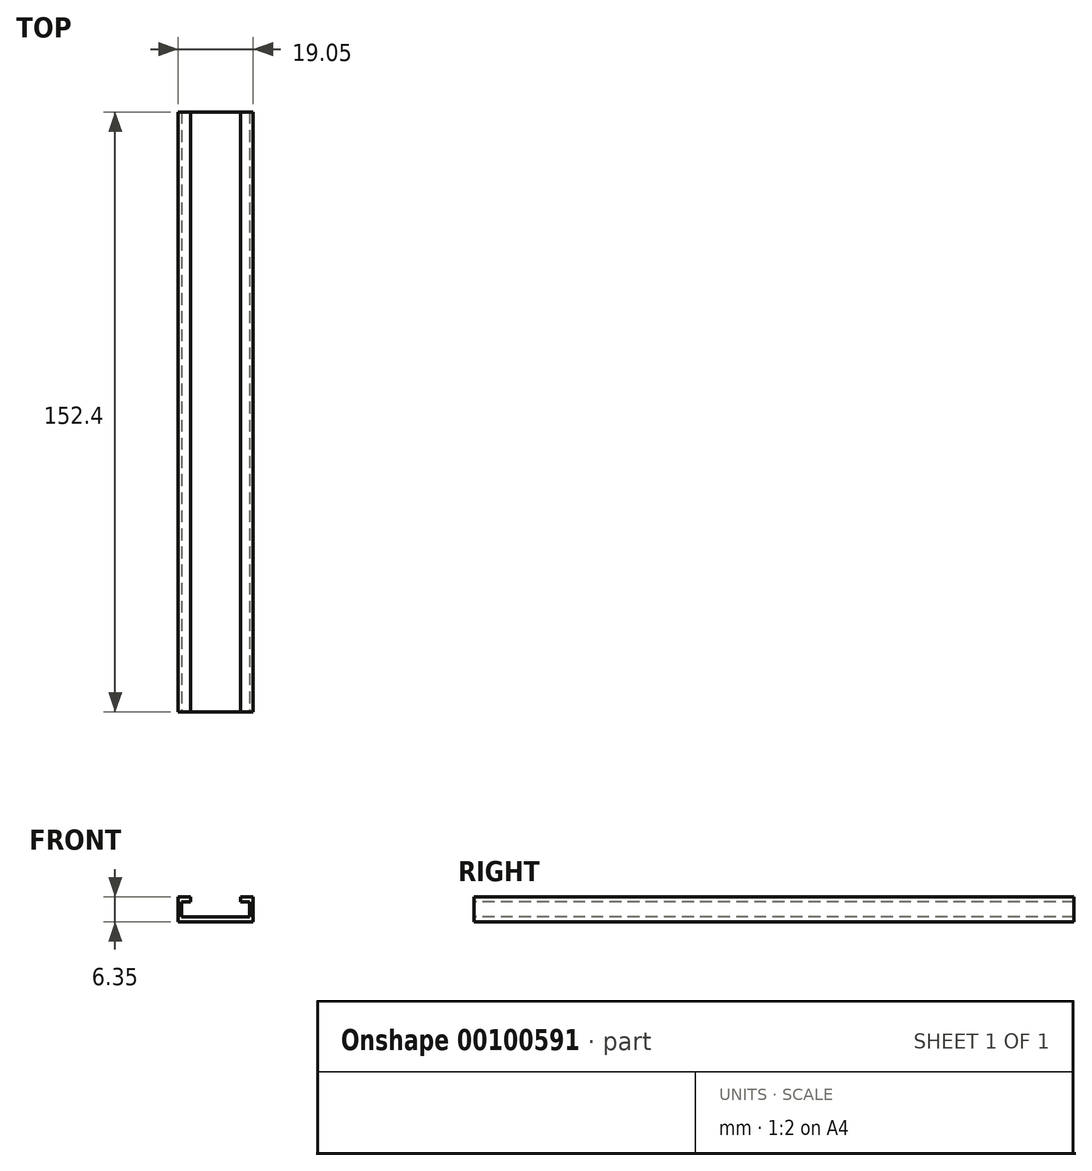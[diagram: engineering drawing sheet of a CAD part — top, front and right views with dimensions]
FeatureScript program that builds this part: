
annotation { "Feature Type Name" : "Feature", "Feature Type Description" : "" }
export const myFeature = defineFeature(function(context is Context, id is Id, definition is map)
    precondition{}
    {
        {
            var Q0;
            Q0=qCreatedBy(makeId("Top.planeOp"),FACE);
            var sketch = newSketch(context, id + "F0", { "sketchPlane" : qUnion([Q0])});
            skLineSegment(sketch, "E0.bottom", {"start": v(-36.41, -40.34) * mm, "end": v(-17.36, -40.34) * mm});
            skLineSegment(sketch, "E0.top", {"start": v(-36.41, 112.06) * mm, "end": v(-17.36, 112.06) * mm});
            skLineSegment(sketch, "E0.left", {"start": v(-36.41, -40.34) * mm, "end": v(-36.41, 112.06) * mm});
            skLineSegment(sketch, "E0.right", {"start": v(-17.36, -40.34) * mm, "end": v(-17.36, 112.06) * mm});
            skSolve(sketch);
        }
        {
            var Q0;
            Q0=makeQuery(id+"F0.imprint","IMPRINT",FACE,{"disambiguationData":[TD([[makeQuery(id+"F0.imprint","IMPRINT",EDGE,{"derivedFrom":sQuery(id+"F0.wireOp",EDGE,"E0.bottom")}),1.0]])]});
            extrude(context, id + "F1", {"entities" : qUnion([Q0]), "depth" : 6.35 * mm});
        }
        {
            var Q0;
            Q0=makeQuery(id+"F1.opExtrude","CAP_FACE",FACE,{"disambiguationData":[OSD([sQuery(id+"F0.wireOp",EDGE,"E0.bottom"),sQuery(id+"F0.wireOp",EDGE,"E0.top"),sQuery(id+"F0.wireOp",EDGE,"E0.left"),sQuery(id+"F0.wireOp",EDGE,"E0.right")])],"isStart":false});
            var sketch = newSketch(context, id + "F2", { "sketchPlane" : qUnion([Q0])});
            skLineSegment(sketch, "E1.bottom", {"start": v(-33.25, -40.34) * mm, "end": v(-20.55, -40.34) * mm});
            skLineSegment(sketch, "E1.top", {"start": v(-33.25, 112.06) * mm, "end": v(-20.55, 112.06) * mm});
            skLineSegment(sketch, "E1.left", {"start": v(-33.25, -40.34) * mm, "end": v(-33.25, 112.06) * mm});
            skLineSegment(sketch, "E1.right", {"start": v(-20.55, -40.34) * mm, "end": v(-20.55, 112.06) * mm});
            skSolve(sketch);
        }
        {
            var Q0;
            Q0=makeQuery(id+"F2.imprint","IMPRINT",FACE,{"disambiguationData":[TD([[makeQuery(id+"F2.imprint","IMPRINT",EDGE,{"derivedFrom":sQuery(id+"F2.wireOp",EDGE,"E1.bottom")}),1.0]])]});
            extrude(context, id + "F3", {"entities" : qUnion([Q0]), "operationType" : NewBodyOperationType.REMOVE, "oppositeDirection" : true, "depth" : 5.08 * mm});
        }
        {
            var Q0;
            Q0=makeQuery(id+"F1.opExtrude","SWEPT_FACE",FACE,{"disambiguationData":[OSD([sQuery(id+"F0.wireOp",EDGE,"E0.bottom")])]});
            var sketch = newSketch(context, id + "F4", { "sketchPlane" : qUnion([Q0])});
            skLineSegment(sketch, "E2.bottom", {"start": v(-33.25, 1.27) * mm, "end": v(-35.54, 1.27) * mm});
            skLineSegment(sketch, "E2.top", {"start": v(-33.25, 5.08) * mm, "end": v(-35.54, 5.08) * mm});
            skLineSegment(sketch, "E2.left", {"start": v(-33.25, 1.27) * mm, "end": v(-33.25, 5.08) * mm});
            skLineSegment(sketch, "E2.right", {"start": v(-35.54, 1.27) * mm, "end": v(-35.54, 5.08) * mm});
            skLineSegment(sketch, "E3.bottom", {"start": v(-20.55, 1.27) * mm, "end": v(-18.27, 1.27) * mm});
            skLineSegment(sketch, "E3.top", {"start": v(-20.55, 5.08) * mm, "end": v(-18.27, 5.08) * mm});
            skLineSegment(sketch, "E3.left", {"start": v(-20.55, 1.27) * mm, "end": v(-20.55, 5.08) * mm});
            skLineSegment(sketch, "E3.right", {"start": v(-18.27, 1.27) * mm, "end": v(-18.27, 5.08) * mm});
            skSolve(sketch);
        }
        {
            var Q0;
            Q0=makeQuery(id+"F4.imprint","IMPRINT",FACE,{"disambiguationData":[TD([[makeQuery(id+"F4.imprint","IMPRINT",EDGE,{"derivedFrom":sQuery(id+"F4.wireOp",EDGE,"E2.bottom")}),-1.0]])]});
            var Q1;
            Q1=makeQuery(id+"F4.imprint","IMPRINT",FACE,{"disambiguationData":[TD([[makeQuery(id+"F4.imprint","IMPRINT",EDGE,{"derivedFrom":sQuery(id+"F4.wireOp",EDGE,"E3.bottom")}),1.0]])]});
            extrude(context, id + "F5", {"entities" : qUnion([Q0, Q1]), "operationType" : NewBodyOperationType.REMOVE, "oppositeDirection" : true, "depth" : 152.4 * mm});
        }
    });
